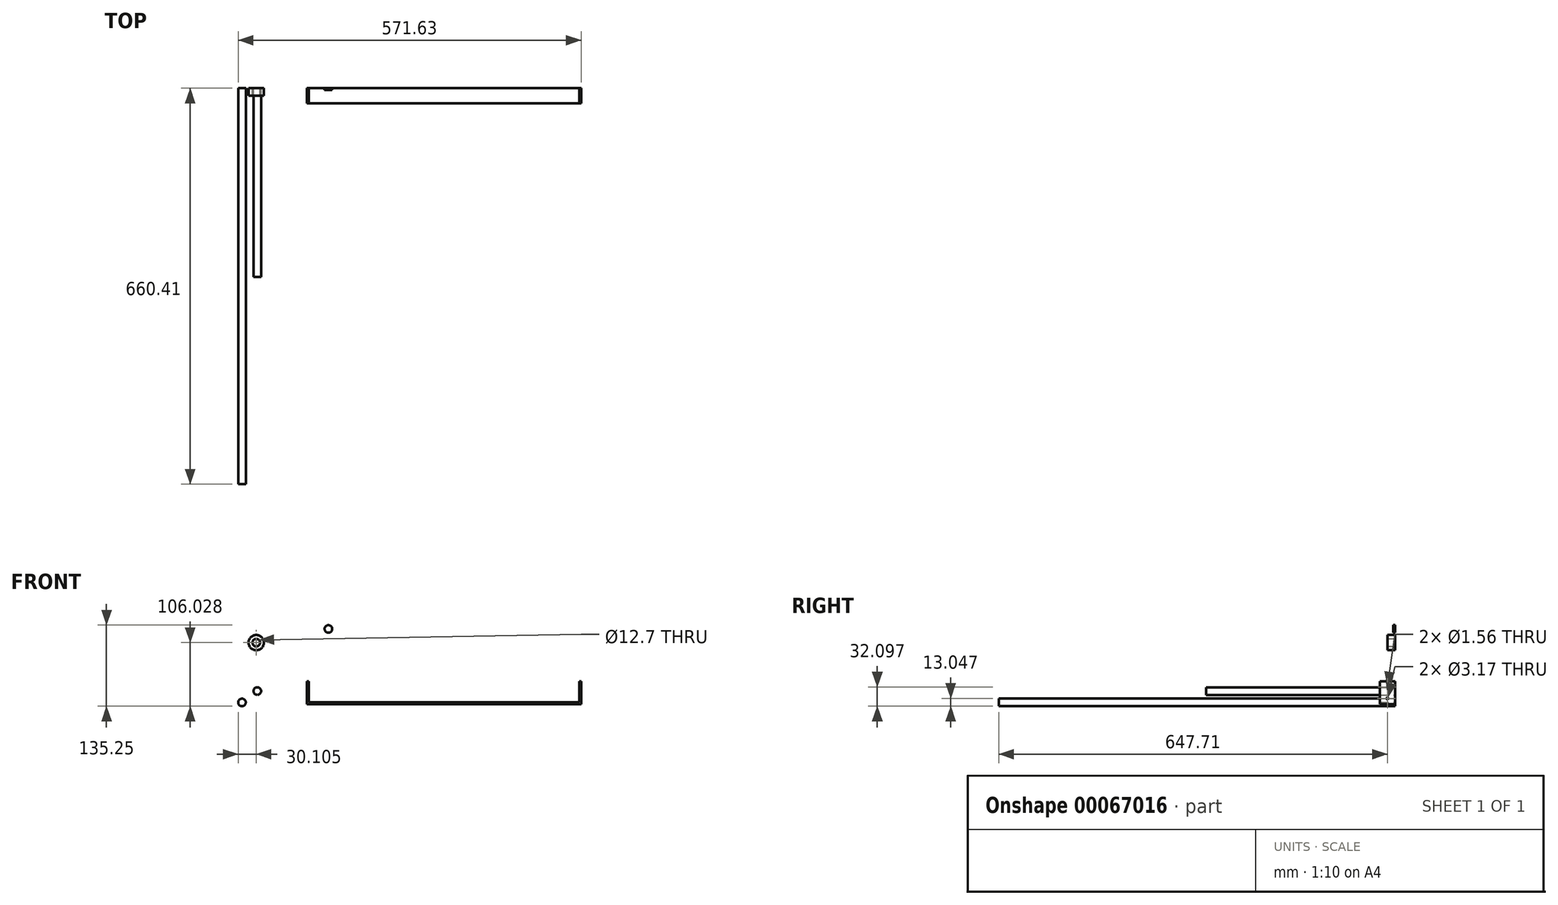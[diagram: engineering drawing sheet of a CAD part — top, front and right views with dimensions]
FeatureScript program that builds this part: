
annotation { "Feature Type Name" : "Feature", "Feature Type Description" : "" }
export const myFeature = defineFeature(function(context is Context, id is Id, definition is map)
    precondition{}
    {
        {
            var Q0;
            Q0=qCreatedBy(makeId("Front.planeOp"),FACE);
            var sketch = newSketch(context, id + "F0", { "sketchPlane" : qUnion([Q0])});
            skCircle(sketch, "E0", {"center": v(-39.33, 38.15) * mm, "radius": 6.35 * mm});
            skCircle(sketch, "E1", {"center": v(-39.33, 38.15) * mm, "radius": 12.7 * mm});
            skCircle(sketch, "E2", {"center": v(-37.64, -42.56) * mm, "radius": 6.35 * mm});
            skLineSegment(sketch, "E3.bottom", {"start": v(4.75, 73.72) * mm, "end": v(309.55, 73.72) * mm});
            skLineSegment(sketch, "E3.top", {"start": v(4.75, 48.32) * mm, "end": v(309.55, 48.32) * mm});
            skLineSegment(sketch, "E3.left", {"start": v(4.75, 73.72) * mm, "end": v(4.75, 48.32) * mm});
            skLineSegment(sketch, "E3.right", {"start": v(309.55, 73.72) * mm, "end": v(309.55, 48.32) * mm});
            skLineSegment(sketch, "E4", {"start": v(44.99, -26.26) * mm, "end": v(44.99, -64.36) * mm});
            skLineSegment(sketch, "E5", {"start": v(44.99, -64.36) * mm, "end": v(502.19, -64.36) * mm});
            skLineSegment(sketch, "E6", {"start": v(502.19, -64.36) * mm, "end": v(502.19, -26.26) * mm});
            skLineSegment(sketch, "E7", {"start": v(502.19, -26.26) * mm, "end": v(499.01, -26.26) * mm});
            skLineSegment(sketch, "E8", {"start": v(499.01, -26.26) * mm, "end": v(499.01, -61.18) * mm});
            skLineSegment(sketch, "E9", {"start": v(499.01, -61.18) * mm, "end": v(48.16, -61.18) * mm});
            skLineSegment(sketch, "E10", {"start": v(48.16, -61.18) * mm, "end": v(48.16, -26.26) * mm});
            skLineSegment(sketch, "E11", {"start": v(48.16, -26.26) * mm, "end": v(44.99, -26.26) * mm});
            skLineSegment(sketch, "E12", {"start": v(273.59, -64.36) * mm, "end": v(273.59, -61.18) * mm, "construction": true});
            skCircle(sketch, "E13", {"center": v(-63.1, -61.53) * mm, "radius": 6.35 * mm});
            skSolve(sketch);
        }
        {
            var Q0;
            Q0=makeQuery(id+"F0.imprint","IMPRINT",FACE,{"disambiguationData":[TD([[makeQuery(id+"F0.imprint","IMPRINT",EDGE,{"derivedFrom":sQuery(id+"F0.wireOp",EDGE,"E4")}),1.0]])]});
            extrude(context, id + "F1", {"entities" : qUnion([Q0]), "depth" : 25.4 * mm});
        }
        {
            var Q0;
            Q0=makeQuery(id+"F1.opExtrude","SWEPT_FACE",FACE,{"disambiguationData":[OSD([sQuery(id+"F0.wireOp",EDGE,"E4")])]});
            var sketch = newSketch(context, id + "F2", { "sketchPlane" : qUnion([Q0])});
            skLineSegment(sketch, "E14", {"start": v(25.4, -26.26) * mm, "end": v(0, -64.36) * mm, "construction": true});
            skLineSegment(sketch, "E15", {"start": v(0, -64.36) * mm, "end": v(25.4, -64.36) * mm, "construction": true});
            skLineSegment(sketch, "E16", {"start": v(25.4, -64.36) * mm, "end": v(0, -26.26) * mm, "construction": true});
            skLineSegment(sketch, "E17", {"start": v(0, -26.26) * mm, "end": v(0, -45.3) * mm, "construction": true});
            skLineSegment(sketch, "E18", {"start": v(0, -45.3) * mm, "end": v(25.4, -45.3) * mm, "construction": true});
            skLineSegment(sketch, "E19", {"start": v(25.4, -45.3) * mm, "end": v(0, -26.26) * mm, "construction": true});
            skLineSegment(sketch, "E20", {"start": v(0, -45.3) * mm, "end": v(25.4, -26.26) * mm, "construction": true});
            skCircle(sketch, "E21", {"center": v(12.7, -54.83) * mm, "radius": 1.59 * mm});
            skCircle(sketch, "E22", {"center": v(12.7, -35.78) * mm, "radius": 0.78 * mm});
            skLineSegment(sketch, "E23", {"start": v(25.4, -45.3) * mm, "end": v(0, -64.36) * mm, "construction": true});
            skSolve(sketch);
        }
        {
            var Q0;
            Q0=makeQuery(id+"F2.imprint","IMPRINT",FACE,{"disambiguationData":[TD([[makeQuery(id+"F2.imprint","IMPRINT",EDGE,{"derivedFrom":sQuery(id+"F2.wireOp",EDGE,"E21")}),1.0]])]});
            var Q1;
            Q1=makeQuery(id+"F2.imprint","IMPRINT",FACE,{"disambiguationData":[TD([[makeQuery(id+"F2.imprint","IMPRINT",EDGE,{"derivedFrom":sQuery(id+"F2.wireOp",EDGE,"E22")}),1.0]])]});
            extrude(context, id + "F3", {"entities" : qUnion([Q0, Q1]), "operationType" : NewBodyOperationType.REMOVE, "endBound" : BoundingType.THROUGH_ALL, "oppositeDirection" : true, "depth" : 25.4 * mm});
        }
        {
            var Q0;
            Q0=makeQuery(id+"F0.imprint","IMPRINT",FACE,{"disambiguationData":[TD([[makeQuery(id+"F0.imprint","IMPRINT",EDGE,{"derivedFrom":sQuery(id+"F0.wireOp",EDGE,"E3.bottom")}),-1.0]])]});
            extrude(context, id + "F4", {"entities" : qUnion([Q0]), "depth" : 3.17 * mm});
        }
        {
            var Q0;
            Q0=makeQuery(id+"F0.imprint","IMPRINT",FACE,{"disambiguationData":[TD([[makeQuery(id+"F0.imprint","IMPRINT",EDGE,{"derivedFrom":sQuery(id+"F0.wireOp",EDGE,"E0")}),-1.0]])]});
            extrude(context, id + "F5", {"entities" : qUnion([Q0]), "depth" : 12.7 * mm});
        }
        {
            var Q0;
            Q0=makeQuery(id+"F0.imprint","IMPRINT",FACE,{"disambiguationData":[TD([[makeQuery(id+"F0.imprint","IMPRINT",EDGE,{"derivedFrom":sQuery(id+"F0.wireOp",EDGE,"E2")}),1.0]])]});
            extrude(context, id + "F6", {"entities" : qUnion([Q0]), "depth" : 314.96 * mm});
        }
        {
            var Q0;
            Q0=makeQuery(id+"F0.imprint","IMPRINT",FACE,{"disambiguationData":[TD([[makeQuery(id+"F0.imprint","IMPRINT",EDGE,{"derivedFrom":sQuery(id+"F0.wireOp",EDGE,"E3.bottom")}),-1.0]])]});
            var sketch = newSketch(context, id + "F7", { "sketchPlane" : qUnion([Q0])});
            skLineSegment(sketch, "E24.0", {"start": v(4.75, 73.72) * mm, "end": v(309.55, 73.72) * mm});
            skLineSegment(sketch, "E24.1", {"start": v(309.55, 73.72) * mm, "end": v(309.55, 48.32) * mm});
            skLineSegment(sketch, "E24.2", {"start": v(4.75, 48.32) * mm, "end": v(309.55, 48.32) * mm});
            skLineSegment(sketch, "E24.3", {"start": v(4.75, 73.72) * mm, "end": v(4.75, 48.32) * mm});
            skLineSegment(sketch, "E25", {"start": v(309.55, 73.72) * mm, "end": v(4.75, 48.32) * mm, "construction": true});
            skLineSegment(sketch, "E26", {"start": v(4.75, 73.72) * mm, "end": v(309.55, 48.32) * mm, "construction": true});
            skLineSegment(sketch, "E27", {"start": v(309.55, 61.02) * mm, "end": v(4.75, 61.02) * mm, "construction": true});
            skLineSegment(sketch, "E28", {"start": v(157.15, 73.72) * mm, "end": v(157.15, 61.02) * mm, "construction": true});
            skLineSegment(sketch, "E29", {"start": v(157.15, 61.02) * mm, "end": v(157.15, 48.32) * mm, "construction": true});
            skLineSegment(sketch, "E30", {"start": v(157.15, 73.72) * mm, "end": v(309.55, 48.32) * mm, "construction": true});
            skLineSegment(sketch, "E31", {"start": v(157.15, 73.72) * mm, "end": v(4.75, 48.32) * mm, "construction": true});
            skCircle(sketch, "E32", {"center": v(233.35, 61.02) * mm, "radius": 6.35 * mm});
            skCircle(sketch, "E33.MirrorC", {"center": v(80.95, 61.02) * mm, "radius": 6.35 * mm});
            skSolve(sketch);
        }
        {
            var Q0;
            Q0=makeQuery(id+"F4.opExtrude","CAP_FACE",FACE,{"disambiguationData":[OSD([sQuery(id+"F0.wireOp",EDGE,"E3.bottom"),sQuery(id+"F0.wireOp",EDGE,"E3.top"),sQuery(id+"F0.wireOp",EDGE,"E3.left"),sQuery(id+"F0.wireOp",EDGE,"E3.right")])],"isStart":false});
            var sketch = newSketch(context, id + "F8", { "sketchPlane" : qUnion([Q0])});
            skCircle(sketch, "E34.0", {"center": v(233.35, 61.02) * mm, "radius": 6.35 * mm});
            skCircle(sketch, "E34.1", {"center": v(80.95, 61.02) * mm, "radius": 6.35 * mm});
            skSolve(sketch);
        }
        {
            var Q0;
            Q0=makeQuery(id+"F8.imprint","IMPRINT",FACE,{"disambiguationData":[TD([[makeQuery(id+"F8.imprint","IMPRINT",EDGE,{"derivedFrom":sQuery(id+"F8.wireOp",EDGE,"E34.0")}),1.0]])]});
            var Q1;
            Q1=makeQuery(id+"F8.imprint","IMPRINT",FACE,{"disambiguationData":[TD([[makeQuery(id+"F8.imprint","IMPRINT",EDGE,{"derivedFrom":sQuery(id+"F8.wireOp",EDGE,"E34.1")}),-1.0]])]});
            extrude(context, id + "F9", {"entities" : qUnion([Q0, Q1]), "operationType" : NewBodyOperationType.REMOVE, "endBound" : BoundingType.THROUGH_ALL, "oppositeDirection" : true, "depth" : 25.4 * mm});
        }
        {
            var Q0;
            Q0=makeQuery(id+"F0.imprint","IMPRINT",FACE,{"disambiguationData":[TD([[makeQuery(id+"F0.imprint","IMPRINT",EDGE,{"derivedFrom":sQuery(id+"F0.wireOp",EDGE,"E13")}),1.0]])]});
            extrude(context, id + "F10", {"entities" : qUnion([Q0]), "depth" : 660.4 * mm});
        }
    });
